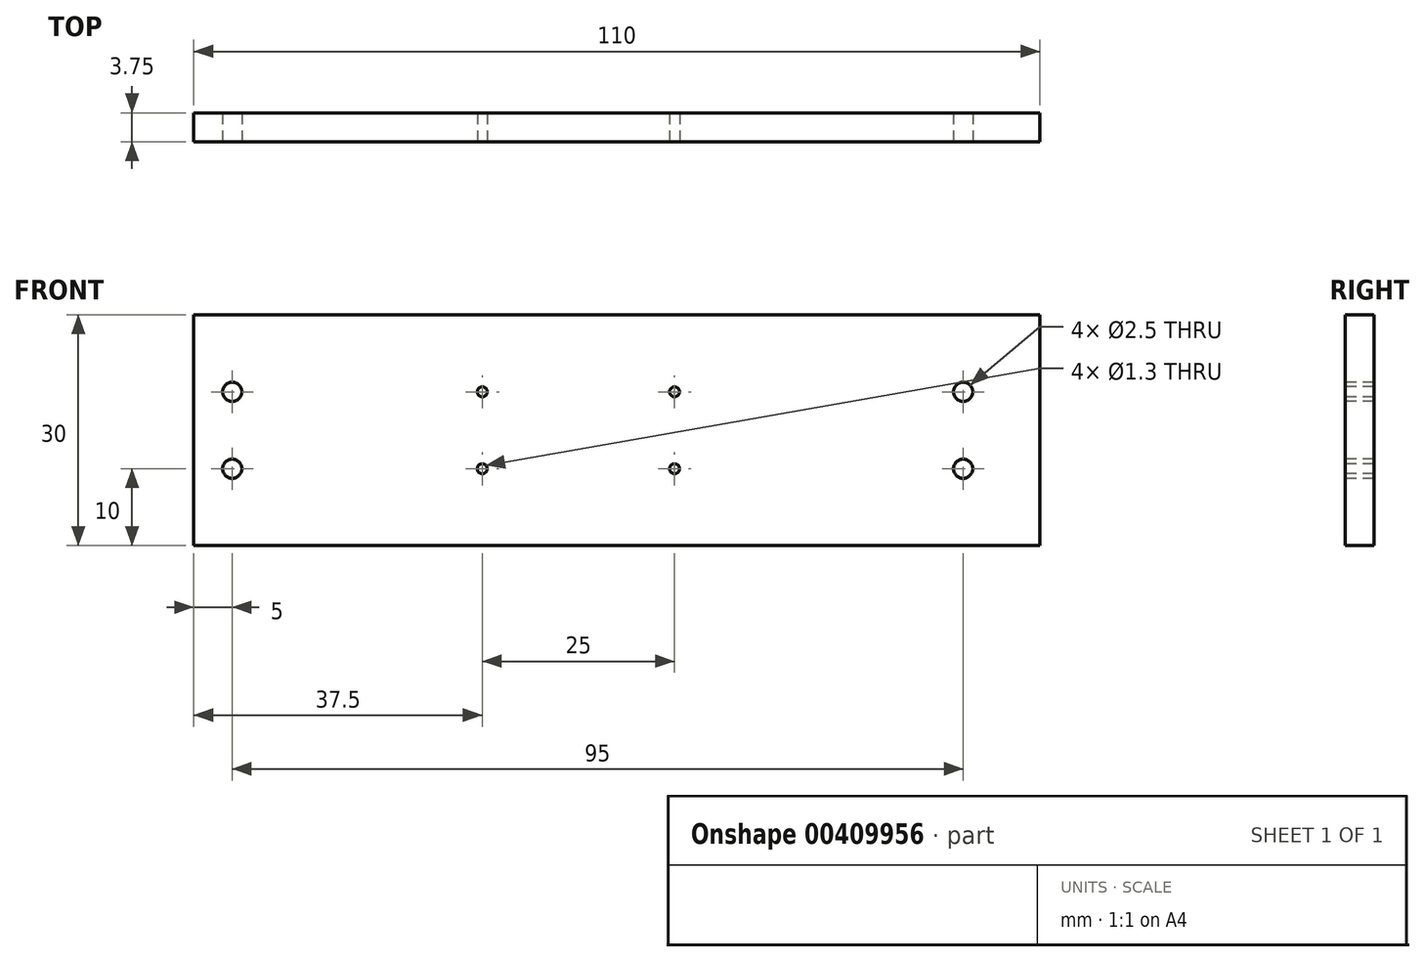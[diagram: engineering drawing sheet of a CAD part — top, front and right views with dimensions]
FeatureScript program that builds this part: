
annotation { "Feature Type Name" : "Feature", "Feature Type Description" : "" }
export const myFeature = defineFeature(function(context is Context, id is Id, definition is map)
    precondition{}
    {
        {
            var Q0;
            Q0=qCreatedBy(makeId("Front.planeOp"),FACE);
            var sketch = newSketch(context, id + "F0", { "sketchPlane" : qUnion([Q0])});
            skLineSegment(sketch, "E0", {"start": v(0, 0) * mm, "end": v(0, 15) * mm});
            skLineSegment(sketch, "E1", {"start": v(0, 15) * mm, "end": v(110, 15) * mm});
            skLineSegment(sketch, "E2", {"start": v(110, 15) * mm, "end": v(110, 0) * mm});
            skLineSegment(sketch, "E3", {"start": v(110, 0) * mm, "end": v(0, 0) * mm});
            skLineSegment(sketch, "E4", {"start": v(60, 63.06) * mm, "end": v(60, -24.68) * mm, "construction": true});
            skLineSegment(sketch, "E5.MirrorCS", {"start": v(110, -15) * mm, "end": v(110, 0) * mm});
            skLineSegment(sketch, "E6.MirrorCS", {"start": v(60, -63.06) * mm, "end": v(60, 24.68) * mm, "construction": true});
            skLineSegment(sketch, "E7.MirrorCS", {"start": v(0, -15) * mm, "end": v(110, -15) * mm});
            skLineSegment(sketch, "E8.MirrorCS", {"start": v(0, 0) * mm, "end": v(0, -15) * mm});
            skSolve(sketch);
        }
        {
            var Q0;
            Q0 = qSketchRegion(id + "F0", true);
            extrude(context, id + "F1", {"entities" : qUnion([Q0]), "depth" : 3.75 * mm});
        }
        {
            var Q0;
            Q0=makeQuery(id+"F1.opExtrude","CAP_FACE",FACE,{"disambiguationData":[OSD([sQuery(id+"F0.wireOp",EDGE,"E0"),sQuery(id+"F0.wireOp",EDGE,"E1"),sQuery(id+"F0.wireOp",EDGE,"E2"),sQuery(id+"F0.wireOp",EDGE,"E5.MirrorCS"),sQuery(id+"F0.wireOp",EDGE,"E7.MirrorCS"),sQuery(id+"F0.wireOp",EDGE,"E8.MirrorCS")])],"isStart":false});
            var sketch = newSketch(context, id + "F2", { "sketchPlane" : qUnion([Q0])});
            skLineSegment(sketch, "E9", {"start": v(0, 0) * mm, "end": v(110, 0) * mm, "construction": true});
            skLineSegment(sketch, "E10", {"start": v(0, 5) * mm, "end": v(110, 5) * mm, "construction": true});
            skLineSegment(sketch, "E11", {"start": v(0, -5) * mm, "end": v(110, -5) * mm, "construction": true});
            skCircle(sketch, "E12", {"center": v(5, 5) * mm, "radius": 1.25 * mm});
            skCircle(sketch, "E13", {"center": v(100, 5) * mm, "radius": 1.25 * mm});
            skCircle(sketch, "E14", {"center": v(62.5, 5) * mm, "radius": 0.65 * mm});
            skCircle(sketch, "E15", {"center": v(37.5, 5) * mm, "radius": 0.65 * mm});
            skCircle(sketch, "E16.MirrorC", {"center": v(5, -5) * mm, "radius": 1.25 * mm});
            skCircle(sketch, "E17.MirrorC", {"center": v(37.5, -5) * mm, "radius": 0.65 * mm});
            skCircle(sketch, "E18.MirrorC", {"center": v(62.5, -5) * mm, "radius": 0.65 * mm});
            skCircle(sketch, "E19.MirrorC", {"center": v(100, -5) * mm, "radius": 1.25 * mm});
            skSolve(sketch);
        }
        {
            var Q0;
            Q0 = qSketchRegion(id + "F2", true);
            extrude(context, id + "F3", {"entities" : qUnion([Q0]), "operationType" : NewBodyOperationType.REMOVE, "oppositeDirection" : true, "depth" : 25 * mm});
        }
    });
